# Revit family: Haworth_Compose_Panel_Tile
name_source: partatom
category: Furniture Systems
revit_build: Autodesk Revit 2018 (Build: 20170223_1515(x64)
units: mm (PartAtom-declared; Revit-internal decimal feet)

## family parameters
Always vertical = Yes
Cut with Voids When Loaded = No
OmniClass Number = 23.40.70.14.64.21
OmniClass Title = Systems Furniture
Part Type = Normal
Room Calculation Point = No
Round Connector Dimension = Use Diameter
Shared = No
Work Plane-Based = No

## types (63) — shared parameters
Assembly Code = E2020500
Description = Haworth - Compose Panel - Accessories External - Mount
Manufacturer = Haworth
Markerboard Tray Finish = Haworth _ Metal _ Brushed Aluminum
Max. Height = 32"
Max. Width = 72"
Min. Height = 16"
Min. Width = 24"
Min/Max Width = 24-60 in. @ 6 in. Increments
Model = External Mount Tile
Panel Finish = Haworth _ Markerboard _ White
Revision Number = 5
Size = Verify Final Dim. w/ Haworth
Sustainability Info = http://media.haworth.com
URL = www.haworth.com
URL - Product = http://www.haworth.com
Warranty = http://www.haworth.com

## per-type parameters (varying)
| type | Actual Height | Actual Width | Custom Size | Height | Markerboard | Min/Max Height | Panel Depth | Panel Height | Panel Width | Slat Tile | Tackboard | Width |
| Markerboard 24w 16h | 16" | 24" | No | 16" | Yes | 16, 24, 32 in. | 5/8" | 16" | 24" | No | No | 24" |
| Markerboard 30w 16h | 16" | 30" | No | 16" | Yes | 16, 24, 32 in. | 5/8" | 16" | 30" | No | No | 30" |
| Markerboard 36w 16h | 16" | 36" | No | 16" | Yes | 16, 24, 32 in. | 5/8" | 16" | 36" | No | No | 36" |
| Markerboard 42w 16h | 16" | 42" | No | 16" | Yes | 16, 24, 32 in. | 5/8" | 16" | 42" | No | No | 42" |
| Markerboard 48w 16h | 16" | 48" | No | 16" | Yes | 16, 24, 32 in. | 5/8" | 16" | 48" | No | No | 48" |
| Markerboard 54w 16h | 16" | 54" | No | 16" | Yes | 16, 24, 32 in. | 5/8" | 16" | 54" | No | No | 54" |
| Markerboard 60w 16h | 16" | 60" | No | 16" | Yes | 16, 24, 32 in. | 5/8" | 16" | 60" | No | No | 60" |
| Markerboard 66w 16h | 16" | 66" | Yes | 16" | Yes | 16, 24, 32 in. | 5/8" | 16" | 66" | No | No | 66" |
| Markerboard 72w 16h | 16" | 72" | Yes | 16" | Yes | 16, 24, 32 in. | 5/8" | 16" | 72" | No | No | 72" |
| Tackboard 24w 16h | 16" | 24" | No | 16" | No | 16 in. | 5/8" | 16" | 24" | No | Yes | 24" |
| Tackboard 30w 16h | 16" | 30" | No | 16" | No | 16 in. | 5/8" | 16" | 30" | No | Yes | 30" |
| Tackboard 36w 16h | 16" | 36" | No | 16" | No | 16 in. | 5/8" | 16" | 36" | No | Yes | 36" |
| Tackboard 42w 16h | 16" | 42" | No | 16" | No | 16 in. | 5/8" | 16" | 42" | No | Yes | 42" |
| Tackboard 48w 16h | 16" | 48" | No | 16" | No | 16 in. | 5/8" | 16" | 48" | No | Yes | 48" |
| Tackboard 54w 16h | 16" | 54" | No | 16" | No | 16 in. | 5/8" | 16" | 54" | No | Yes | 54" |
| Tackboard 60w 16h | 16" | 60" | No | 16" | No | 16 in. | 5/8" | 16" | 60" | No | Yes | 60" |
| Tackboard 66w 16h | 16" | 66" | Yes | 16" | No | 16 in. | 5/8" | 16" | 66" | No | Yes | 66" |
| Tackboard 72w 16h | 16" | 72" | Yes | 16" | No | 16 in. | 5/8" | 16" | 72" | No | Yes | 72" |
| Tackboard 24w 24h | 24" | 24" | No | 24" | No | 16 in. | 5/8" | 24" | 24" | No | Yes | 24" |
| Tackboard 30w 24h | 24" | 30" | No | 24" | No | 16 in. | 5/8" | 24" | 30" | No | Yes | 30" |
| Tackboard 36w 24h | 24" | 36" | No | 24" | No | 16 in. | 5/8" | 24" | 36" | No | Yes | 36" |
| Tackboard 42w 24h | 24" | 42" | No | 24" | No | 16 in. | 5/8" | 24" | 42" | No | Yes | 42" |
| Tackboard 48w 24h | 24" | 48" | No | 24" | No | 16 in. | 5/8" | 24" | 48" | No | Yes | 48" |
| Tackboard 54w 24h | 24" | 54" | No | 24" | No | 16 in. | 5/8" | 24" | 54" | No | Yes | 54" |
| Tackboard 60w 24h | 24" | 60" | No | 24" | No | 16 in. | 5/8" | 24" | 60" | No | Yes | 60" |
| Tackboard 66w 24h | 24" | 66" | Yes | 24" | No | 16 in. | 5/8" | 24" | 66" | No | Yes | 66" |
| Tackboard 72w 24h | 24" | 72" | Yes | 24" | No | 16 in. | 5/8" | 24" | 72" | No | Yes | 72" |
| Tackboard 24w 32h | 32" | 24" | No | 32" | No | 16 in. | 5/8" | 32" | 24" | No | Yes | 24" |
| Tackboard 30w 32h | 32" | 30" | No | 32" | No | 16 in. | 5/8" | 32" | 30" | No | Yes | 30" |
| Tackboard 36w 32h | 32" | 36" | No | 32" | No | 16 in. | 5/8" | 32" | 36" | No | Yes | 36" |
| Tackboard 42w 32h | 32" | 42" | No | 32" | No | 16 in. | 5/8" | 32" | 42" | No | Yes | 42" |
| Tackboard 48w 32h | 32" | 48" | No | 32" | No | 16 in. | 5/8" | 32" | 48" | No | Yes | 48" |
| Tackboard 54w 32h | 32" | 54" | No | 32" | No | 16 in. | 5/8" | 32" | 54" | No | Yes | 54" |
| Tackboard 60w 32h | 32" | 60" | No | 32" | No | 16 in. | 5/8" | 32" | 60" | No | Yes | 60" |
| Tackboard 66w 32h | 32" | 66" | Yes | 32" | No | 16 in. | 5/8" | 32" | 66" | No | Yes | 66" |
| Tackboard 72w 32h | 32" | 72" | Yes | 32" | No | 16 in. | 5/8" | 32" | 72" | No | Yes | 72" |
| Slat Tile 24w 16h | 16" | 24" | No | 16" | No | 16 in. | 3/8" | 16" | 24" | Yes | No | 24" |
| Slat Tile 30w 16h | 16" | 30" | No | 16" | No | 16 in. | 3/8" | 16" | 30" | Yes | No | 30" |
| Slat Tile 36w 16h | 16" | 36" | No | 16" | No | 16 in. | 3/8" | 16" | 36" | Yes | No | 36" |
| Slat Tile 42w 16h | 16" | 42" | No | 16" | No | 16 in. | 3/8" | 16" | 42" | Yes | No | 42" |
| Slat Tile 48w 16h | 16" | 48" | No | 16" | No | 16 in. | 3/8" | 16" | 48" | Yes | No | 48" |
| Slat Tile 54w 16h | 16" | 54" | No | 16" | No | 16 in. | 3/8" | 16" | 54" | Yes | No | 54" |
| Slat Tile 60w 16h | 16" | 60" | No | 16" | No | 16 in. | 3/8" | 16" | 60" | Yes | No | 60" |
| Slat Tile 66w 16h | 16" | 66" | Yes | 16" | No | 16 in. | 3/8" | 16" | 66" | Yes | No | 66" |
| Slat Tile 72w 16h | 16" | 72" | Yes | 16" | No | 16 in. | 3/8" | 16" | 72" | Yes | No | 72" |
| Slat Tile 24w 24h | 24" | 24" | No | 24" | No | 16 in. | 3/8" | 24" | 24" | Yes | No | 24" |
| Slat Tile 30w 24h | 24" | 30" | No | 24" | No | 16 in. | 3/8" | 24" | 30" | Yes | No | 30" |
| Slat Tile 36w 24h | 24" | 36" | No | 24" | No | 16 in. | 3/8" | 24" | 36" | Yes | No | 36" |
| Slat Tile 42w 24h | 24" | 42" | No | 24" | No | 16 in. | 3/8" | 24" | 42" | Yes | No | 42" |
| Slat Tile 48w 24h | 24" | 48" | No | 24" | No | 16 in. | 3/8" | 24" | 48" | Yes | No | 48" |
| Slat Tile 54w 24h | 24" | 54" | No | 24" | No | 16 in. | 3/8" | 24" | 54" | Yes | No | 54" |
| Slat Tile 60w 24h | 24" | 60" | No | 24" | No | 16 in. | 3/8" | 24" | 60" | Yes | No | 60" |
| Slat Tile 66w 24h | 24" | 66" | Yes | 24" | No | 16 in. | 3/8" | 24" | 66" | Yes | No | 66" |
| Slat Tile 72w 24h | 24" | 72" | Yes | 24" | No | 16 in. | 3/8" | 24" | 72" | Yes | No | 72" |
| Slat Tile 24w 32h | 32" | 24" | No | 32" | No | 16 in. | 3/8" | 32" | 24" | Yes | No | 24" |
| Slat Tile 30w 32h | 32" | 30" | No | 32" | No | 16 in. | 3/8" | 32" | 30" | Yes | No | 30" |
| Slat Tile 36w 32h | 32" | 36" | No | 32" | No | 16 in. | 3/8" | 32" | 36" | Yes | No | 36" |
| Slat Tile 42w 32h | 32" | 42" | No | 32" | No | 16 in. | 3/8" | 32" | 42" | Yes | No | 42" |
| Slat Tile 48w 32h | 32" | 48" | No | 32" | No | 16 in. | 3/8" | 32" | 48" | Yes | No | 48" |
| Slat Tile 54w 32h | 32" | 54" | No | 32" | No | 16 in. | 3/8" | 32" | 54" | Yes | No | 54" |
| Slat Tile 60w 32h | 32" | 60" | No | 32" | No | 16 in. | 3/8" | 32" | 60" | Yes | No | 60" |
| Slat Tile 66w 32h | 32" | 66" | Yes | 32" | No | 16 in. | 3/8" | 32" | 66" | Yes | No | 66" |
| Slat Tile 72w 32h | 32" | 72" | Yes | 32" | No | 16 in. | 3/8" | 32" | 72" | Yes | No | 72" |

## geometry (parser evidence)
native form markers: Blend x2, Sweep x2
no freeform markers — native parametric forms only
